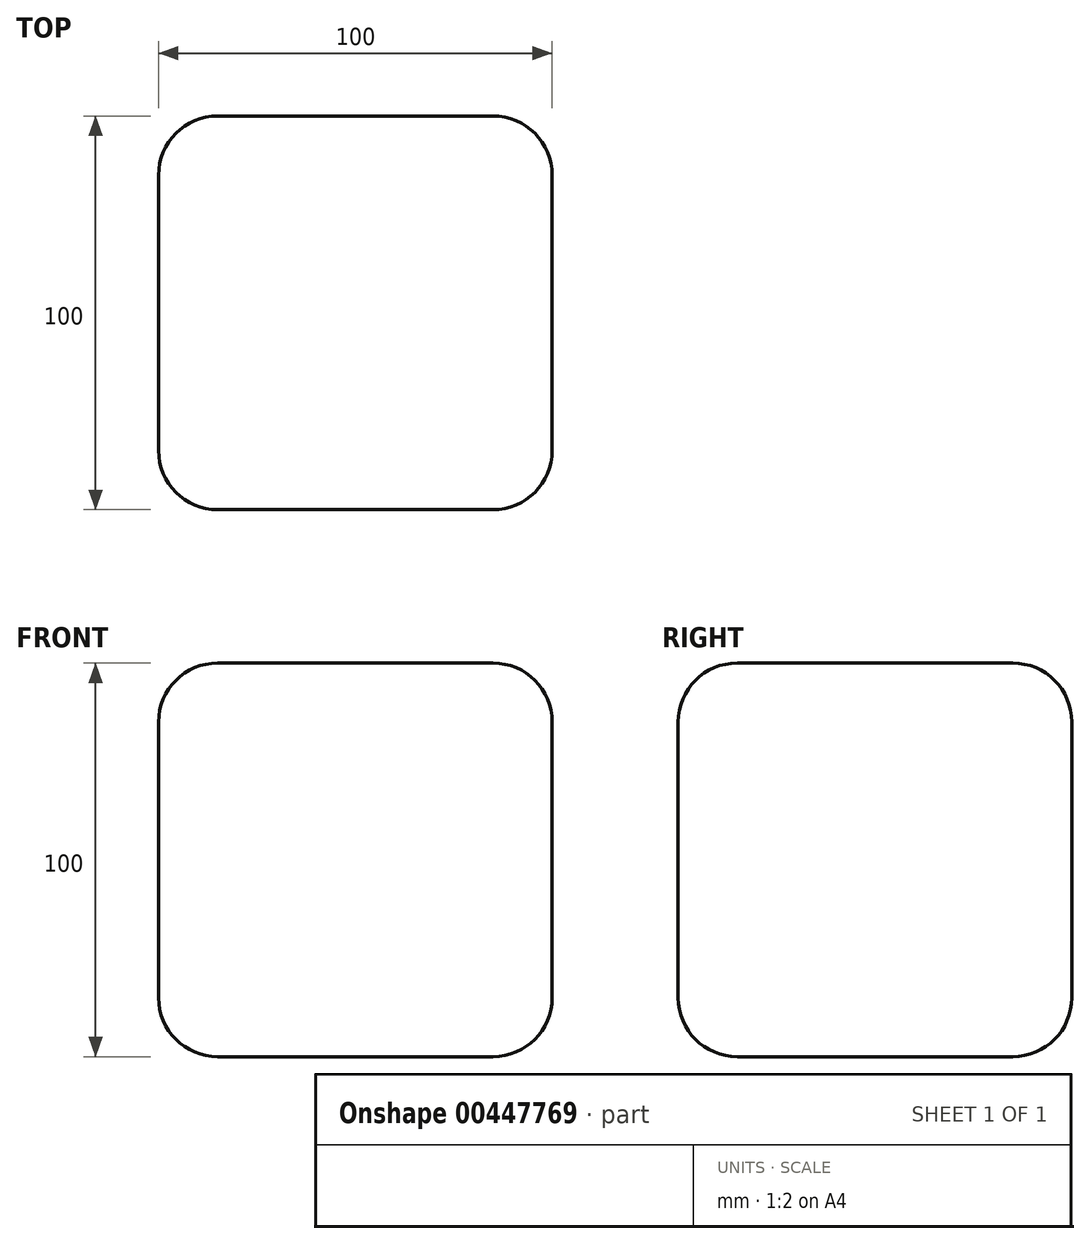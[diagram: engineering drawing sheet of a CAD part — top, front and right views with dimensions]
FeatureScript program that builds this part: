
annotation { "Feature Type Name" : "Feature", "Feature Type Description" : "" }
export const myFeature = defineFeature(function(context is Context, id is Id, definition is map)
    precondition{}
    {
        {
            var Q0;
            Q0=qCreatedBy(makeId("Top.planeOp"),FACE);
            var sketch = newSketch(context, id + "F0", { "sketchPlane" : qUnion([Q0])});
            skLineSegment(sketch, "E0.bottom", {"start": v(0, 0) * mm, "end": v(100, 0) * mm});
            skLineSegment(sketch, "E0.top", {"start": v(0, 100) * mm, "end": v(100, 100) * mm});
            skLineSegment(sketch, "E0.left", {"start": v(0, 0) * mm, "end": v(0, 100) * mm});
            skLineSegment(sketch, "E0.right", {"start": v(100, 0) * mm, "end": v(100, 100) * mm});
            skPoint(sketch, "E1.centerSnap0", {"position": v(50, 100) * mm});
            skSolve(sketch);
        }
        {
            var Q0;
            Q0=makeQuery(id+"F0.imprint","IMPRINT",FACE,{"disambiguationData":[TD([[makeQuery(id+"F0.imprint","IMPRINT",EDGE,{"derivedFrom":sQuery(id+"F0.wireOp",EDGE,"E0.bottom")}),1.0]])]});
            extrude(context, id + "F1", {"entities" : qUnion([Q0]), "depth" : 100 * mm});
        }
        {
            var Q0;
            Q0=makeQuery(id+"F1.opExtrude","CAP_EDGE",EDGE,{"disambiguationData":[OSD([sQuery(id+"F0.wireOp",EDGE,"E0.left")])],"isStart":false});
            var Q1;
            Q1=makeQuery(id+"F1.opExtrude","CAP_FACE",FACE,{"disambiguationData":[OSD([sQuery(id+"F0.wireOp",EDGE,"E0.bottom"),sQuery(id+"F0.wireOp",EDGE,"E0.top"),sQuery(id+"F0.wireOp",EDGE,"E0.left"),sQuery(id+"F0.wireOp",EDGE,"E0.right")])],"isStart":false});
            var Q2;
            Q2=makeQuery(id+"F1.opExtrude","SWEPT_FACE",FACE,{"disambiguationData":[OSD([sQuery(id+"F0.wireOp",EDGE,"E0.bottom")])]});
            var Q3;
            Q3=makeQuery(id+"F1.opExtrude","SWEPT_FACE",FACE,{"disambiguationData":[OSD([sQuery(id+"F0.wireOp",EDGE,"E0.right")])]});
            var Q4;
            Q4=makeQuery(id+"F1.opExtrude","SWEPT_FACE",FACE,{"disambiguationData":[OSD([sQuery(id+"F0.wireOp",EDGE,"E0.left")])]});
            var Q5;
            Q5=makeQuery(id+"F1.opExtrude","SWEPT_FACE",FACE,{"disambiguationData":[OSD([sQuery(id+"F0.wireOp",EDGE,"E0.top")])]});
            var Q6;
            Q6=makeQuery(id+"F1.opExtrude","CAP_FACE",FACE,{"disambiguationData":[OSD([sQuery(id+"F0.wireOp",EDGE,"E0.bottom"),sQuery(id+"F0.wireOp",EDGE,"E0.top"),sQuery(id+"F0.wireOp",EDGE,"E0.left"),sQuery(id+"F0.wireOp",EDGE,"E0.right")])],"isStart":true});
            fillet(context, id + "F2", {"entities" : qUnion([Q0, Q1, Q2, Q3, Q4, Q5, Q6]), "radius" : 15 * mm, "tangentPropagation" : true, "allowEdgeOverflow" : false});
        }
    });
